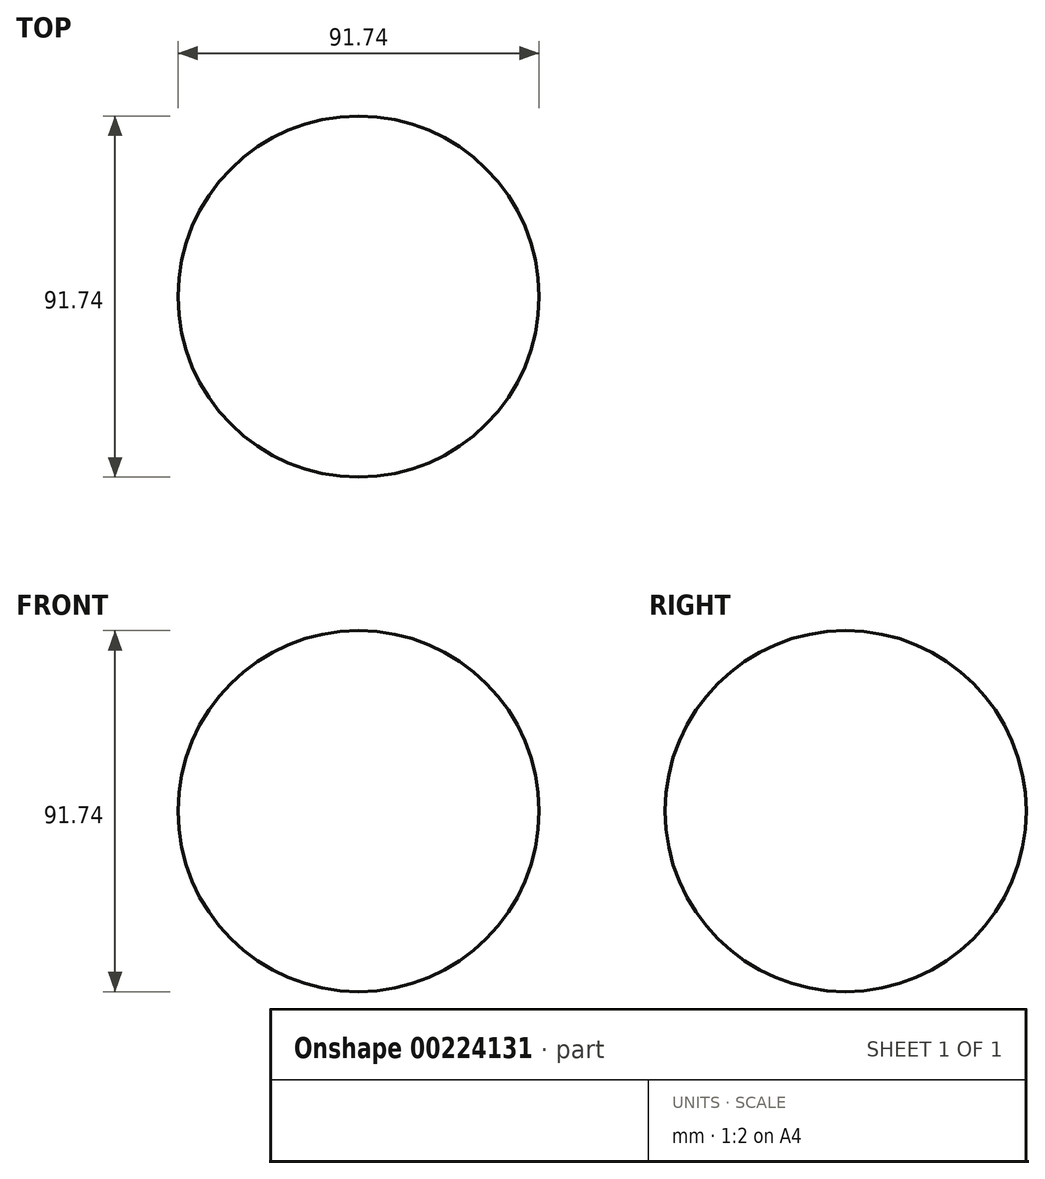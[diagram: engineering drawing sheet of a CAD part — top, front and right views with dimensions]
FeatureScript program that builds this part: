
annotation { "Feature Type Name" : "Feature", "Feature Type Description" : "" }
export const myFeature = defineFeature(function(context is Context, id is Id, definition is map)
    precondition{}
    {
        {
            var Q0;
            Q0=qCreatedBy(makeId("Front.planeOp"),FACE);
            var sketch = newSketch(context, id + "F0", { "sketchPlane" : qUnion([Q0])});
            skCircle(sketch, "E0", {"center": v(0, 0) * mm, "radius": 45.87 * mm});
            skLineSegment(sketch, "E1", {"start": v(0, 45.87) * mm, "end": v(0, -45.87) * mm});
            skSolve(sketch);
        }
        {
            var Q0;
            Q0=qCreatedBy(makeId("Front.planeOp"),FACE);
            var sketch = newSketch(context, id + "F1", { "sketchPlane" : qUnion([Q0])});
            skSolve(sketch);
        }
        {
            var Q0;
            Q0 = qSketchRegion(id + "F1", true);
            var Q1;
            {var subQ0=sQuery(id+"F0.wireOp",EDGE,"E1");Q1=makeQuery(id+"F0.imprint","IMPRINT",FACE,{"disambiguationData":[TD([[makeQuery(id+"F0.imprint","IMPRINT",EDGE,{"derivedFrom":subQ0}),-1.0]])]});}
            var Q2;
            Q2=sQuery(id+"F0.wireOp",EDGE,"E1");
            revolve(context, id + "F2", {"entities" : qUnion([Q0, Q1]), "axis" : qUnion([Q2]), "revolveType" : RevolveType.FULL});
        }
    });
